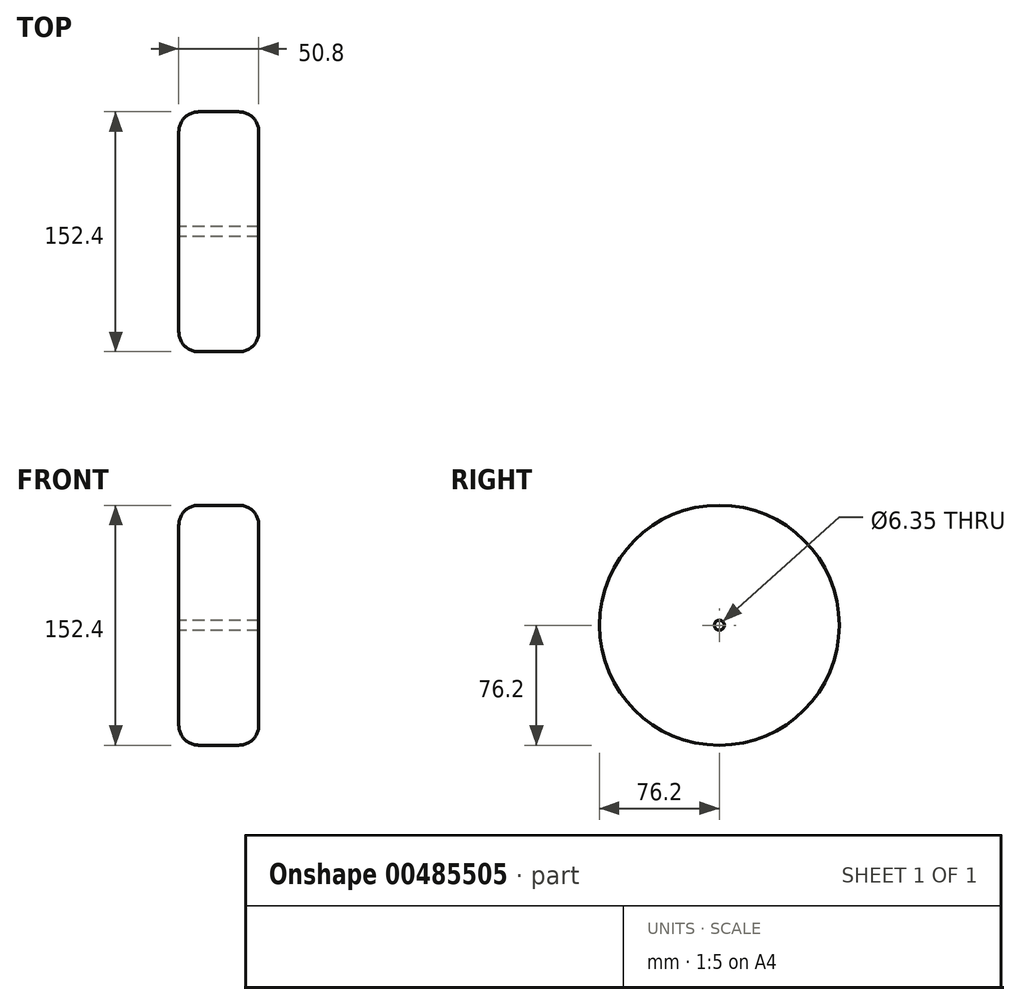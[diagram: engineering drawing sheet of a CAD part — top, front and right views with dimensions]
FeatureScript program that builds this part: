
annotation { "Feature Type Name" : "Feature", "Feature Type Description" : "" }
export const myFeature = defineFeature(function(context is Context, id is Id, definition is map)
    precondition{}
    {
        {
            var Q0;
            Q0=qCreatedBy(makeId("Right.planeOp"),FACE);
            var sketch = newSketch(context, id + "F0", { "sketchPlane" : qUnion([Q0])});
            skCircle(sketch, "E0", {"center": v(0, 0) * mm, "radius": 76.2 * mm});
            skCircle(sketch, "E1", {"center": v(0, 0) * mm, "radius": 3.18 * mm});
            skSolve(sketch);
        }
        {
            var Q0;
            Q0 = qSketchRegion(id + "F0", true);
            extrude(context, id + "F1", {"entities" : qUnion([Q0]), "depth" : 50.8 * mm});
        }
        {
            var Q0;
            Q0=makeQuery(id+"F1.opExtrude","CAP_EDGE",EDGE,{"disambiguationData":[OSD([sQuery(id+"F0.wireOp",EDGE,"E0")])],"isStart":false});
            fillet(context, id + "F2", {"entities" : qUnion([Q0]), "radius" : 12.7 * mm, "tangentPropagation" : true, "allowEdgeOverflow" : false});
        }
        {
            var Q0;
            Q0=makeQuery(id+"F1.opExtrude","CAP_EDGE",EDGE,{"disambiguationData":[OSD([sQuery(id+"F0.wireOp",EDGE,"E0")])],"isStart":true});
            fillet(context, id + "F3", {"entities" : qUnion([Q0]), "radius" : 12.7 * mm, "tangentPropagation" : true, "allowEdgeOverflow" : false});
        }
    });
